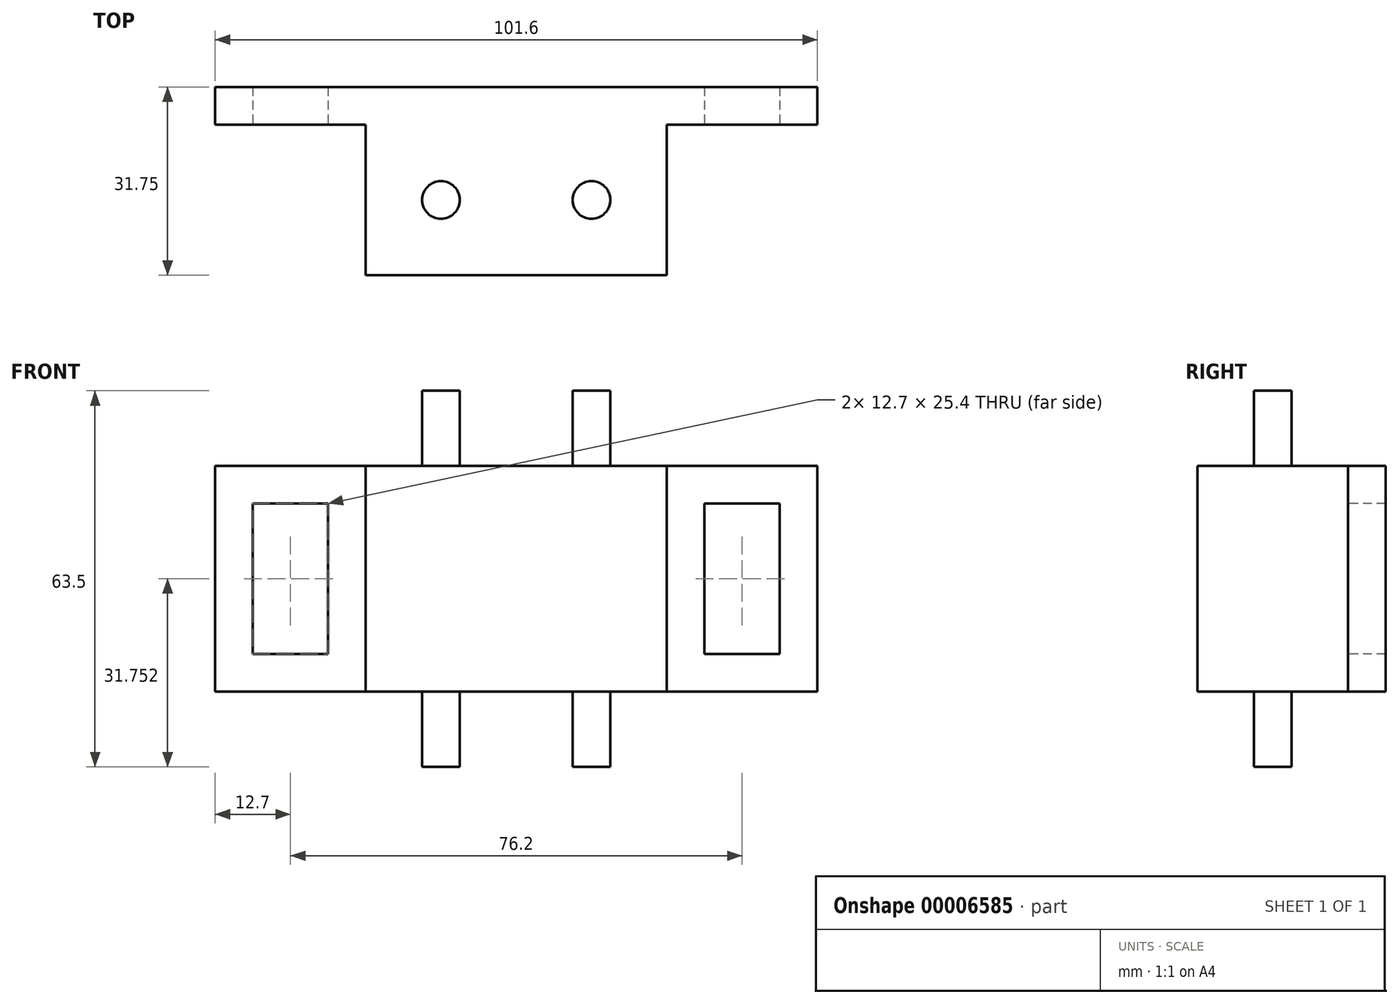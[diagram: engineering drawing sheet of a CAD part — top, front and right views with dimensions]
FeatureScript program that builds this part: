
annotation { "Feature Type Name" : "Feature", "Feature Type Description" : "" }
export const myFeature = defineFeature(function(context is Context, id is Id, definition is map)
    precondition{}
    {
        {
            var Q0;
            Q0=qCreatedBy(makeId("Front.planeOp"),FACE);
            var sketch = newSketch(context, id + "F0", { "sketchPlane" : qUnion([Q0])});
            skLineSegment(sketch, "E0.bottom", {"start": v(-50.8, 19.05) * mm, "end": v(50.8, 19.05) * mm});
            skLineSegment(sketch, "E0.top", {"start": v(-50.8, -19.05) * mm, "end": v(50.8, -19.05) * mm});
            skLineSegment(sketch, "E0.left", {"start": v(-50.8, 19.05) * mm, "end": v(-50.8, -19.05) * mm});
            skLineSegment(sketch, "E0.right", {"start": v(50.8, 19.05) * mm, "end": v(50.8, -19.05) * mm});
            skSolve(sketch);
        }
        {
            var Q0;
            Q0 = qSketchRegion(id + "F0", true);
            extrude(context, id + "F1", {"entities" : qUnion([Q0]), "depth" : 6.35 * mm});
        }
        {
            var Q0;
            Q0=makeQuery(id+"F1.opExtrude","CAP_FACE",FACE,{"disambiguationData":[OSD([sQuery(id+"F0.wireOp",EDGE,"E0.bottom"),sQuery(id+"F0.wireOp",EDGE,"E0.top"),sQuery(id+"F0.wireOp",EDGE,"E0.left"),sQuery(id+"F0.wireOp",EDGE,"E0.right")])],"isStart":false});
            var sketch = newSketch(context, id + "F2", { "sketchPlane" : qUnion([Q0])});
            skLineSegment(sketch, "E1.bottom", {"start": v(-25.4, 19.05) * mm, "end": v(25.4, 19.05) * mm});
            skLineSegment(sketch, "E1.top", {"start": v(-25.4, -19.05) * mm, "end": v(25.4, -19.05) * mm});
            skLineSegment(sketch, "E1.left", {"start": v(-25.4, 19.05) * mm, "end": v(-25.4, -19.05) * mm});
            skLineSegment(sketch, "E1.right", {"start": v(25.4, 19.05) * mm, "end": v(25.4, -19.05) * mm});
            skSolve(sketch);
        }
        {
            var Q0;
            Q0 = qSketchRegion(id + "F2", true);
            extrude(context, id + "F3", {"entities" : qUnion([Q0]), "operationType" : NewBodyOperationType.ADD, "depth" : 25.4 * mm});
        }
        {
            var Q0;
            Q0=makeQuery(id+"F3.boolean.opBoolean","MERGE",FACE,{"derivedFrom":[makeQuery(id+"F1.opExtrude","SWEPT_FACE",FACE,{"disambiguationData":[OSD([sQuery(id+"F0.wireOp",EDGE,"E0.bottom")])]}),makeQuery(id+"F3.opExtrude","SWEPT_FACE",FACE,{"disambiguationData":[OSD([sQuery(id+"F2.wireOp",EDGE,"E1.bottom")])]})]});
            var sketch = newSketch(context, id + "F4", { "sketchPlane" : qUnion([Q0])});
            skCircle(sketch, "E2", {"center": v(-12.7, -19.05) * mm, "radius": 3.18 * mm});
            skCircle(sketch, "E3", {"center": v(12.7, -19.05) * mm, "radius": 3.18 * mm});
            skSolve(sketch);
        }
        {
            var Q0;
            Q0 = qSketchRegion(id + "F4", true);
            extrude(context, id + "F5", {"entities" : qUnion([Q0]), "operationType" : NewBodyOperationType.ADD, "depth" : 12.7 * mm});
        }
        {
            var Q0;
            Q0 = qSketchRegion(id + "F4", true);
            extrude(context, id + "F6", {"entities" : qUnion([Q0]), "operationType" : NewBodyOperationType.ADD, "oppositeDirection" : true, "depth" : 50.8 * mm});
        }
        {
            var Q0;
            {var subQ0=sQuery(id+"F0.wireOp",EDGE,"E0.bottom");var subQ1=sQuery(id+"F0.wireOp",EDGE,"E0.top");var subQ2=sQuery(id+"F0.wireOp",EDGE,"E0.left");Q0=makeQuery(id+"F3.boolean.opBoolean","SPLIT",FACE,{"disambiguationData":[TD([makeQuery(id+"F1.opExtrude","SWEPT_FACE",FACE,{"disambiguationData":[OSD([subQ2])]})])],"derivedFrom":makeQuery(id+"F1.opExtrude","CAP_FACE",FACE,{"disambiguationData":[OSD([subQ0,subQ1,subQ2,sQuery(id+"F0.wireOp",EDGE,"E0.right")])],"isStart":false})});}
            var sketch = newSketch(context, id + "F7", { "sketchPlane" : qUnion([Q0])});
            skLineSegment(sketch, "E4.bottom", {"start": v(-44.45, 12.7) * mm, "end": v(-31.75, 12.7) * mm});
            skLineSegment(sketch, "E4.top", {"start": v(-44.45, -12.7) * mm, "end": v(-31.75, -12.7) * mm});
            skLineSegment(sketch, "E4.left", {"start": v(-44.45, 12.7) * mm, "end": v(-44.45, -12.7) * mm});
            skLineSegment(sketch, "E4.right", {"start": v(-31.75, 12.7) * mm, "end": v(-31.75, -12.7) * mm});
            skLineSegment(sketch, "E5.bottom", {"start": v(31.75, 12.7) * mm, "end": v(44.45, 12.7) * mm});
            skLineSegment(sketch, "E5.top", {"start": v(31.75, -12.7) * mm, "end": v(44.45, -12.7) * mm});
            skLineSegment(sketch, "E5.left", {"start": v(31.75, 12.7) * mm, "end": v(31.75, -12.7) * mm});
            skLineSegment(sketch, "E5.right", {"start": v(44.45, 12.7) * mm, "end": v(44.45, -12.7) * mm});
            skSolve(sketch);
        }
        {
            var Q0;
            Q0 = qSketchRegion(id + "F7", true);
            extrude(context, id + "F8", {"entities" : qUnion([Q0]), "operationType" : NewBodyOperationType.REMOVE, "oppositeDirection" : true, "depth" : 25.4 * mm});
        }
    });
